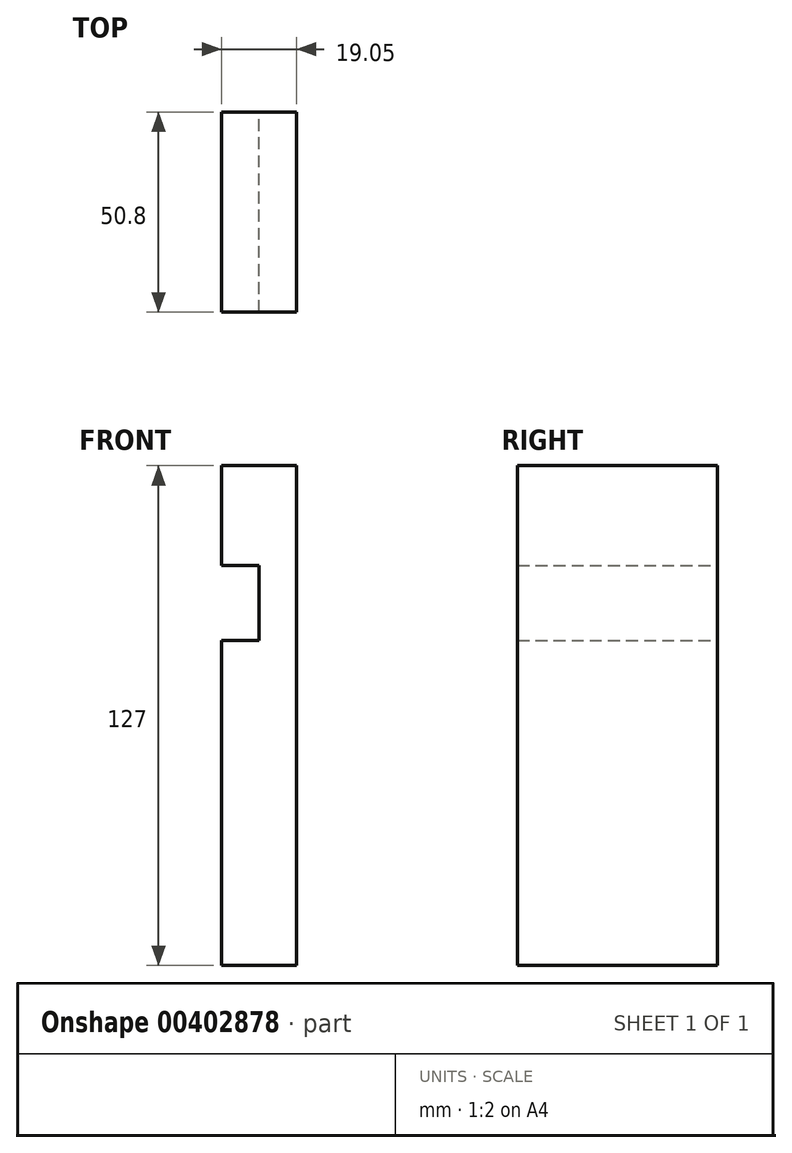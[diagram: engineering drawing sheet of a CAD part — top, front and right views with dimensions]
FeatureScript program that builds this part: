
annotation { "Feature Type Name" : "Feature", "Feature Type Description" : "" }
export const myFeature = defineFeature(function(context is Context, id is Id, definition is map)
    precondition{}
    {
        {
            var Q0;
            Q0=qCreatedBy(makeId("Front.planeOp"),FACE);
            var sketch = newSketch(context, id + "F0", { "sketchPlane" : qUnion([Q0])});
            skLineSegment(sketch, "E0", {"start": v(0, 0) * mm, "end": v(0, 63.5) * mm});
            skLineSegment(sketch, "E1", {"start": v(0, 0) * mm, "end": v(0, -63.5) * mm});
            skLineSegment(sketch, "E2", {"start": v(0, 63.5) * mm, "end": v(-19.05, 63.5) * mm});
            skLineSegment(sketch, "E3", {"start": v(-19.05, 63.5) * mm, "end": v(-19.05, 38.1) * mm});
            skLineSegment(sketch, "E4", {"start": v(-19.05, 38.1) * mm, "end": v(-9.52, 38.1) * mm});
            skLineSegment(sketch, "E5", {"start": v(-9.52, 38.1) * mm, "end": v(-9.52, 19.05) * mm});
            skLineSegment(sketch, "E6", {"start": v(-9.52, 19.05) * mm, "end": v(-19.05, 19.05) * mm});
            skLineSegment(sketch, "E7", {"start": v(0, -63.5) * mm, "end": v(-19.05, -63.5) * mm});
            skLineSegment(sketch, "E8", {"start": v(-19.05, 19.05) * mm, "end": v(-19.05, -65.6) * mm});
            skSolve(sketch);
        }
        {
            var Q0;
            Q0 = qSketchRegion(id + "F0", true);
            extrude(context, id + "F1", {"entities" : qUnion([Q0]), "depth" : 50.8 * mm});
        }
    });
